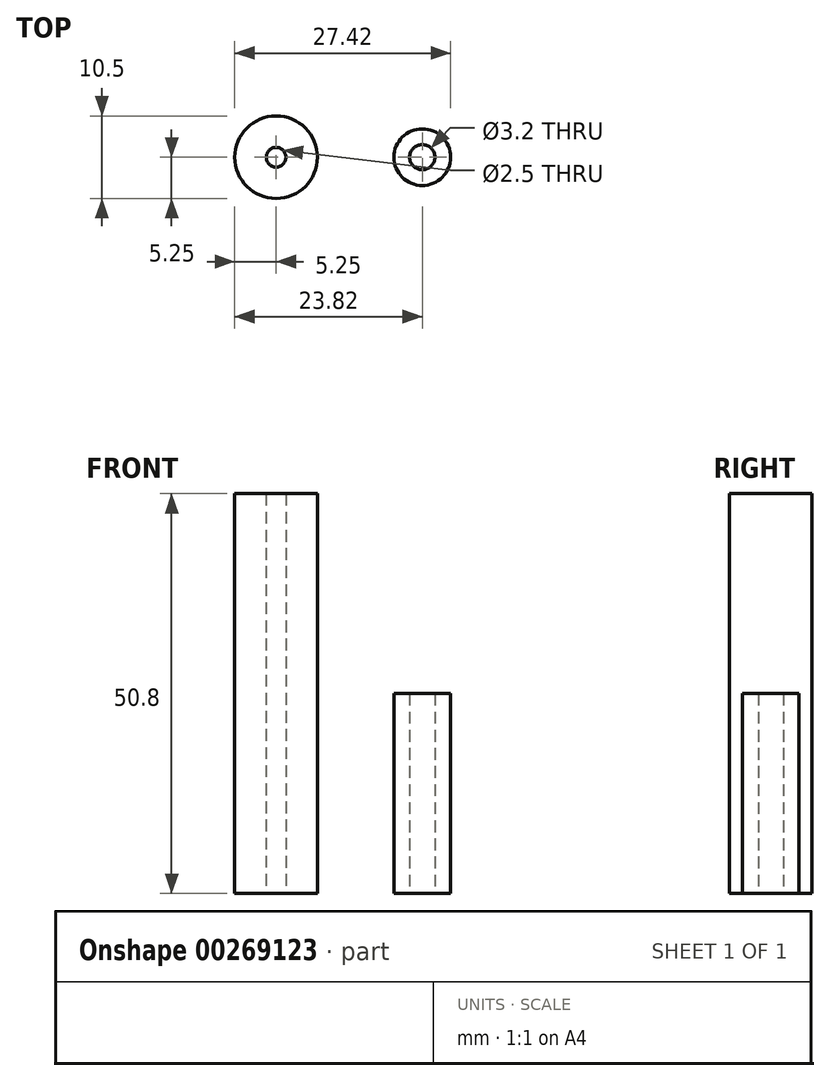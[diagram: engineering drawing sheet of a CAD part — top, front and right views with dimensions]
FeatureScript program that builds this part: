
annotation { "Feature Type Name" : "Feature", "Feature Type Description" : "" }
export const myFeature = defineFeature(function(context is Context, id is Id, definition is map)
    precondition{}
    {
        {
            var Q0;
            Q0=qCreatedBy(makeId("Top.planeOp"),FACE);
            var sketch = newSketch(context, id + "F0", { "sketchPlane" : qUnion([Q0])});
            skCircle(sketch, "E0", {"center": v(0, 0) * mm, "radius": 5.25 * mm});
            skCircle(sketch, "E1", {"center": v(0, 0) * mm, "radius": 1.25 * mm});
            skSolve(sketch);
        }
        {
            var Q0;
            Q0 = qSketchRegion(id + "F0", true);
            var Q1;
            Q1 = qConstructionFilter(qBodyType(qCreatedBy(id + "F0" ,EDGE), BodyType.WIRE), ConstructionObject.NO);
            extrude(context, id + "F1", {"entities" : qUnion([Q0]), "surfaceEntities" : qUnion([Q1]), "depth" : 50.8 * mm});
        }
        {
            var Q0;
            Q0=qCreatedBy(makeId("Top.planeOp"),FACE);
            var sketch = newSketch(context, id + "F2", { "sketchPlane" : qUnion([Q0])});
            skCircle(sketch, "E2", {"center": v(18.57, 0) * mm, "radius": 3.6 * mm});
            skCircle(sketch, "E3", {"center": v(18.57, 0) * mm, "radius": 1.6 * mm});
            skSolve(sketch);
        }
        {
            var Q0;
            Q0=makeQuery(id+"F2.imprint","IMPRINT",FACE,{"disambiguationData":[TD([[makeQuery(id+"F2.imprint","IMPRINT",EDGE,{"derivedFrom":sQuery(id+"F2.wireOp",EDGE,"E2")}),1.0]])]});
            extrude(context, id + "F3", {"entities" : qUnion([Q0]), "depth" : 25.4 * mm});
        }
    });
